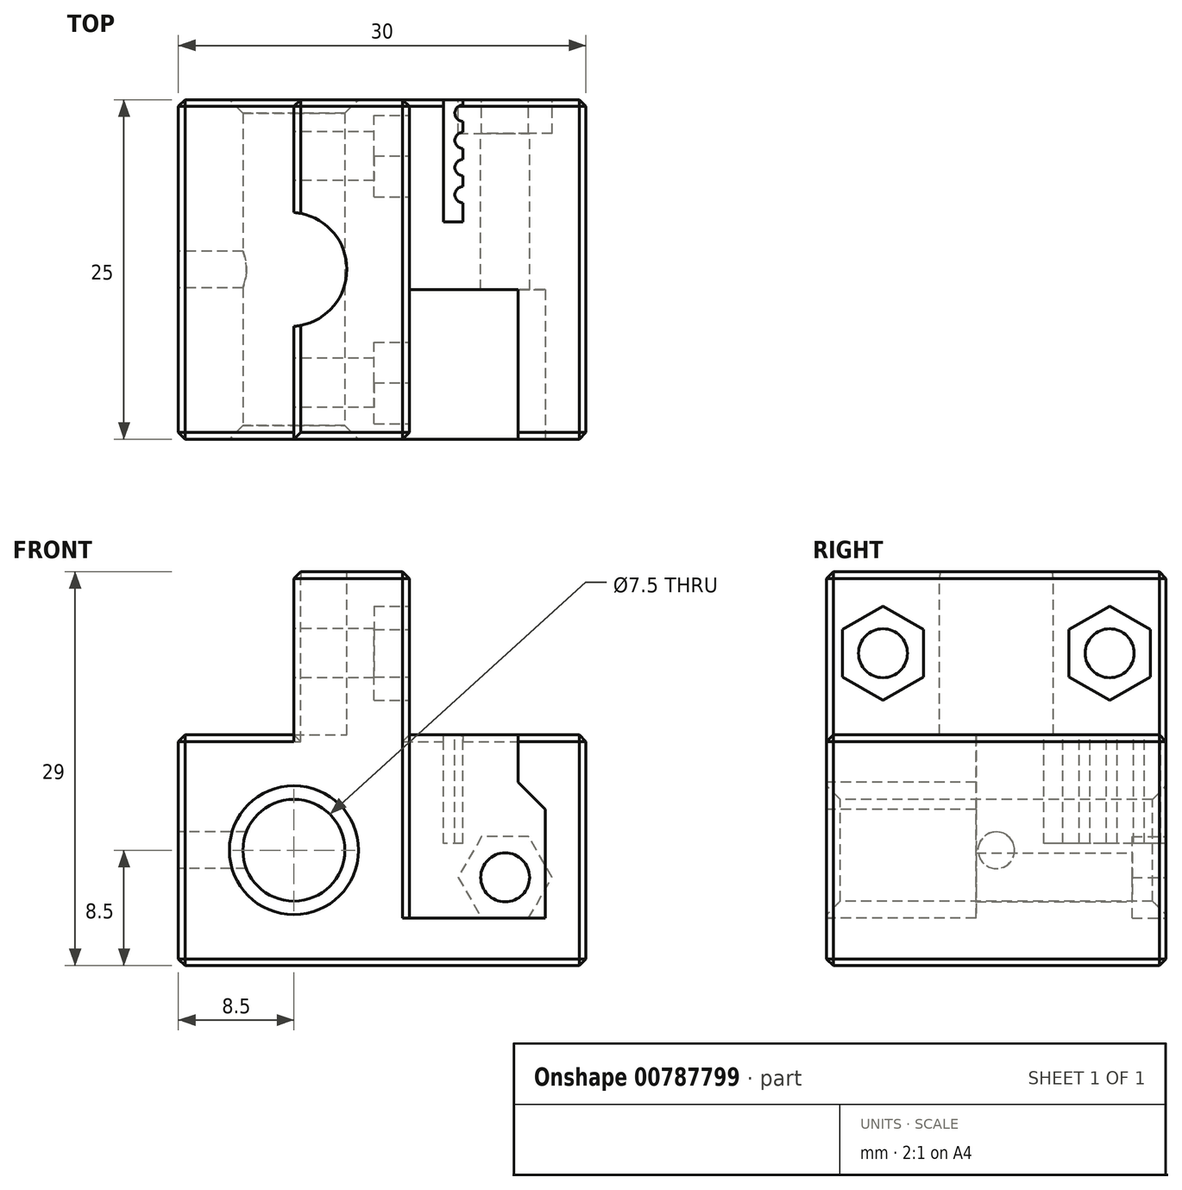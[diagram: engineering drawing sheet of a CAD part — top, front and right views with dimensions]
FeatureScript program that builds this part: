
annotation { "Feature Type Name" : "Feature", "Feature Type Description" : "" }
export const myFeature = defineFeature(function(context is Context, id is Id, definition is map)
    precondition{}
    {
        {
            var Q0;
            Q0=qCreatedBy(makeId("Top.planeOp"),FACE);
            var sketch = newSketch(context, id + "F0", { "sketchPlane" : qUnion([Q0])});
            skLineSegment(sketch, "E0.bottom", {"start": v(15, 12.5) * mm, "end": v(-15, 12.5) * mm});
            skLineSegment(sketch, "E0.top", {"start": v(15, -12.5) * mm, "end": v(-15, -12.5) * mm});
            skLineSegment(sketch, "E0.left", {"start": v(15, 12.5) * mm, "end": v(15, -12.5) * mm});
            skLineSegment(sketch, "E0.right", {"start": v(-15, 12.5) * mm, "end": v(-15, -12.5) * mm});
            skPoint(sketch, "E0.middle", {"position": v(0, 0) * mm});
            skSolve(sketch);
        }
        {
            var Q0;
            Q0=makeQuery(id+"F0.imprint","IMPRINT",FACE,{"disambiguationData":[TD([[makeQuery(id+"F0.imprint","IMPRINT",EDGE,{"derivedFrom":sQuery(id+"F0.wireOp",EDGE,"E0.bottom")}),1.0]])]});
            extrude(context, id + "F1", {"entities" : qUnion([Q0]), "depth" : 17 * mm, "offsetDistance" : 25 * mm});
        }
        {
            var Q0;
            Q0=makeQuery(id+"F1.opExtrude","SWEPT_FACE",FACE,{"disambiguationData":[OSD([sQuery(id+"F0.wireOp",EDGE,"E0.top")])]});
            var sketch = newSketch(context, id + "F2", { "sketchPlane" : qUnion([Q0])});
            skLineSegment(sketch, "E1", {"start": v(2, 17) * mm, "end": v(10, 17) * mm});
            skLineSegment(sketch, "E2", {"start": v(10, 17) * mm, "end": v(10, 13.5) * mm});
            skLineSegment(sketch, "E3", {"start": v(10, 13.5) * mm, "end": v(12, 11.5) * mm});
            skLineSegment(sketch, "E4", {"start": v(12, 11.5) * mm, "end": v(12, 3.5) * mm});
            skLineSegment(sketch, "E5", {"start": v(12, 3.5) * mm, "end": v(2, 3.5) * mm});
            skLineSegment(sketch, "E6", {"start": v(2, 3.5) * mm, "end": v(2, 17) * mm});
            skSolve(sketch);
        }
        {
            var Q0;
            Q0=makeQuery(id+"F2.imprint","IMPRINT",FACE,{"disambiguationData":[TD([[makeQuery(id+"F2.imprint","IMPRINT",EDGE,{"derivedFrom":sQuery(id+"F2.wireOp",EDGE,"E1")}),1.0]])]});
            extrude(context, id + "F3", {"entities" : qUnion([Q0]), "operationType" : NewBodyOperationType.REMOVE, "oppositeDirection" : true, "depth" : 11 * mm, "offsetDistance" : 25 * mm});
        }
        {
            var Q0;
            Q0=makeQuery(id+"F1.opExtrude","SWEPT_FACE",FACE,{"disambiguationData":[OSD([sQuery(id+"F0.wireOp",EDGE,"E0.top")])]});
            var sketch = newSketch(context, id + "F4", { "sketchPlane" : qUnion([Q0])});
            skCircle(sketch, "E7", {"center": v(-6.5, 8.5) * mm, "radius": 3.75 * mm});
            skPoint(sketch, "E7.centerSnap0", {"position": v(-6.5, 17) * mm});
            skPoint(sketch, "E7.centerSnap1", {"position": v(-15, 8.5) * mm});
            skSolve(sketch);
        }
        {
            var Q0;
            Q0=makeQuery(id+"F4.imprint","IMPRINT",FACE,{"disambiguationData":[TD([[makeQuery(id+"F4.imprint","IMPRINT",EDGE,{"derivedFrom":sQuery(id+"F4.wireOp",EDGE,"E7")}),1.0]])]});
            extrude(context, id + "F5", {"entities" : qUnion([Q0]), "operationType" : NewBodyOperationType.REMOVE, "endBound" : BoundingType.UP_TO_NEXT, "oppositeDirection" : true, "depth" : 25 * mm, "offsetDistance" : 25 * mm});
        }
        {
            var Q0;
            Q0=makeQuery(id+"F1.opExtrude","CAP_FACE",FACE,{"disambiguationData":[OSD([sQuery(id+"F0.wireOp",EDGE,"E0.bottom"),sQuery(id+"F0.wireOp",EDGE,"E0.top"),sQuery(id+"F0.wireOp",EDGE,"E0.left"),sQuery(id+"F0.wireOp",EDGE,"E0.right")])],"isStart":false});
            var sketch = newSketch(context, id + "F6", { "sketchPlane" : qUnion([Q0])});
            skLineSegment(sketch, "E8.bottom", {"start": v(2, -12.5) * mm, "end": v(-6.5, -12.5) * mm});
            skLineSegment(sketch, "E8.top", {"start": v(2, 12.5) * mm, "end": v(-6.5, 12.5) * mm});
            skLineSegment(sketch, "E8.left", {"start": v(2, -12.5) * mm, "end": v(2, 12.5) * mm});
            skLineSegment(sketch, "E8.right", {"start": v(-6.5, -12.5) * mm, "end": v(-6.5, 12.5) * mm});
            skSolve(sketch);
        }
        {
            var Q0;
            {var subQ1=sQuery(id+"F6.wireOp",EDGE,"E8.bottom");Q0=makeQuery(id+"F6.imprint","IMPRINT",FACE,{"disambiguationData":[TD([[makeQuery(id+"F6.imprint","IMPRINT",EDGE,{"derivedFrom":subQ1}),-1.0]])]});}
            extrude(context, id + "F7", {"entities" : qUnion([Q0]), "operationType" : NewBodyOperationType.ADD, "depth" : 12 * mm, "offsetDistance" : 25 * mm});
        }
        {
            var Q0;
            Q0=makeQuery(id+"F7.opExtrude","CAP_FACE",FACE,{"disambiguationData":[OSD([sQuery(id+"F6.wireOp",EDGE,"E8.bottom"),sQuery(id+"F6.wireOp",EDGE,"E8.top"),sQuery(id+"F6.wireOp",EDGE,"E8.left"),sQuery(id+"F6.wireOp",EDGE,"E8.right")])],"isStart":false});
            var sketch = newSketch(context, id + "F8", { "sketchPlane" : qUnion([Q0])});
            skArc(sketch, "E9", {"start": v(-6.5, -4.19) * mm, "mid": v(-2.6, 0) * mm, "end": v(-6.5, 4.19) * mm});
            skPoint(sketch, "E9.centerSnap0", {"position": v(-6.5, 0) * mm});
            skLineSegment(sketch, "E10", {"start": v(-6.5, 4.19) * mm, "end": v(-6.5, -4.19) * mm});
            skSolve(sketch);
        }
        {
            var Q0;
            Q0=makeQuery(id+"F8.imprint","IMPRINT",FACE,{"disambiguationData":[TD([[makeQuery(id+"F8.imprint","IMPRINT",EDGE,{"derivedFrom":sQuery(id+"F8.wireOp",EDGE,"E9")}),1.0]])]});
            extrude(context, id + "F9", {"entities" : qUnion([Q0]), "operationType" : NewBodyOperationType.REMOVE, "oppositeDirection" : true, "depth" : 12 * mm, "offsetDistance" : 25 * mm});
        }
        {
            var Q0;
            {var subQ0=sQuery(id+"F6.wireOp",EDGE,"E8.right");var subQ2=sQuery(id+"F0.wireOp",EDGE,"E0.top");Q0=makeQuery(id+"F9.boolean.opBoolean","SPLIT",FACE,{"disambiguationData":[TD([makeQuery(id+"F1.opExtrude","SWEPT_FACE",FACE,{"disambiguationData":[OSD([subQ2])]})])],"derivedFrom":makeQuery(id+"F7.opExtrude","SWEPT_FACE",FACE,{"disambiguationData":[OSD([subQ0])]})});}
            var sketch = newSketch(context, id + "F10", { "sketchPlane" : qUnion([Q0])});
            skCircle(sketch, "E11", {"center": v(8.34, 23) * mm, "radius": 1.8 * mm});
            skPoint(sketch, "E11.centerSnap0", {"position": v(12.5, 23) * mm});
            skPoint(sketch, "E11.centerSnap1", {"position": v(8.34, 29) * mm});
            skLineSegment(sketch, "E12.0", {"start": v(-4.19, 29) * mm, "end": v(-12.5, 29) * mm});
            skPoint(sketch, "E13.0", {"position": v(-4.19, 23) * mm});
            skCircle(sketch, "E14", {"center": v(-8.34, 23) * mm, "radius": 1.8 * mm});
            skPoint(sketch, "E14.centerSnap0", {"position": v(-8.34, 29) * mm});
            skSolve(sketch);
        }
        {
            var Q0;
            Q0=makeQuery(id+"F10.imprint","IMPRINT",FACE,{"disambiguationData":[TD([[makeQuery(id+"F10.imprint","IMPRINT",EDGE,{"derivedFrom":sQuery(id+"F10.wireOp",EDGE,"E14")}),1.0]])]});
            var Q1;
            Q1=makeQuery(id+"F10.imprint","IMPRINT",FACE,{"disambiguationData":[TD([[makeQuery(id+"F10.imprint","IMPRINT",EDGE,{"derivedFrom":sQuery(id+"F10.wireOp",EDGE,"E11")}),1.0]])]});
            extrude(context, id + "F11", {"entities" : qUnion([Q0, Q1]), "operationType" : NewBodyOperationType.REMOVE, "endBound" : BoundingType.UP_TO_NEXT, "oppositeDirection" : true, "depth" : 25 * mm, "offsetDistance" : 25 * mm});
        }
        {
            var Q0;
            Q0=makeQuery(id+"F7.boolean.opBoolean","MERGE",FACE,{"derivedFrom":[makeQuery(id+"F3.boolean.opBoolean","COPY",FACE,{"derivedFrom":makeQuery(id+"F3.opExtrude","SWEPT_FACE",FACE,{"disambiguationData":[OSD([sQuery(id+"F2.wireOp",EDGE,"E6")])]})}),makeQuery(id+"F7.opExtrude","SWEPT_FACE",FACE,{"disambiguationData":[OSD([sQuery(id+"F6.wireOp",EDGE,"E8.left")])]})]});
            var sketch = newSketch(context, id + "F12", { "sketchPlane" : qUnion([Q0])});
            skCircle(sketch, "E15.cCircle", {"center": v(8.34, 23) * mm, "radius": 3 * mm, "construction": true});
            skLineSegment(sketch, "E15.0", {"start": v(11.34, 24.73) * mm, "end": v(11.34, 21.27) * mm});
            skLineSegment(sketch, "E15.1", {"start": v(11.34, 21.27) * mm, "end": v(8.34, 19.54) * mm});
            skLineSegment(sketch, "E15.2", {"start": v(8.34, 19.54) * mm, "end": v(5.34, 21.27) * mm});
            skLineSegment(sketch, "E15.3", {"start": v(5.34, 21.27) * mm, "end": v(5.34, 24.73) * mm});
            skLineSegment(sketch, "E15.4", {"start": v(5.34, 24.73) * mm, "end": v(8.34, 26.46) * mm});
            skLineSegment(sketch, "E15.5", {"start": v(8.34, 26.46) * mm, "end": v(11.34, 24.73) * mm});
            skPoint(sketch, "E15.0.midPoint", {"position": v(11.34, 23) * mm});
            skCircle(sketch, "E16.cCircle", {"center": v(-8.34, 23) * mm, "radius": 3 * mm, "construction": true});
            skLineSegment(sketch, "E16.0", {"start": v(-5.34, 24.73) * mm, "end": v(-5.34, 21.27) * mm});
            skLineSegment(sketch, "E16.1", {"start": v(-5.34, 21.27) * mm, "end": v(-8.34, 19.54) * mm});
            skLineSegment(sketch, "E16.2", {"start": v(-8.34, 19.54) * mm, "end": v(-11.34, 21.27) * mm});
            skLineSegment(sketch, "E16.3", {"start": v(-11.34, 21.27) * mm, "end": v(-11.34, 24.73) * mm});
            skLineSegment(sketch, "E16.4", {"start": v(-11.34, 24.73) * mm, "end": v(-8.34, 26.46) * mm});
            skLineSegment(sketch, "E16.5", {"start": v(-8.34, 26.46) * mm, "end": v(-5.34, 24.73) * mm});
            skPoint(sketch, "E16.0.midPoint", {"position": v(-5.34, 23) * mm});
            skSolve(sketch);
        }
        {
            var Q0;
            Q0=makeQuery(id+"F12.imprint","IMPRINT",FACE,{"disambiguationData":[TD([[makeQuery(id+"F12.imprint","IMPRINT",EDGE,{"derivedFrom":sQuery(id+"F12.wireOp",EDGE,"E15.0")}),-1.0]])]});
            var Q1;
            Q1=makeQuery(id+"F12.imprint","IMPRINT",FACE,{"disambiguationData":[TD([[makeQuery(id+"F12.imprint","IMPRINT",EDGE,{"derivedFrom":sQuery(id+"F12.wireOp",EDGE,"E16.0")}),-1.0]])]});
            extrude(context, id + "F13", {"entities" : qUnion([Q0, Q1]), "operationType" : NewBodyOperationType.REMOVE, "oppositeDirection" : true, "depth" : 2.6 * mm, "offsetDistance" : 25 * mm});
        }
        {
            var Q0;
            {var subQ0=sQuery(id+"F0.wireOp",EDGE,"E0.left");var subQ1=sQuery(id+"F0.wireOp",EDGE,"E0.top");var subQ4=sQuery(id+"F0.wireOp",EDGE,"E0.bottom");Q0=makeQuery(id+"F7.boolean.opBoolean","SPLIT",FACE,{"disambiguationData":[TD([makeQuery(id+"F1.opExtrude","SWEPT_FACE",FACE,{"disambiguationData":[OSD([subQ0])]})])],"derivedFrom":makeQuery(id+"F1.opExtrude","CAP_FACE",FACE,{"disambiguationData":[OSD([subQ4,subQ1,subQ0,sQuery(id+"F0.wireOp",EDGE,"E0.right")])],"isStart":false})});}
            var sketch = newSketch(context, id + "F14", { "sketchPlane" : qUnion([Q0])});
            skLineSegment(sketch, "E17.bottom", {"start": v(4.5, 12.5) * mm, "end": v(5.95, 12.5) * mm});
            skLineSegment(sketch, "E17.top", {"start": v(4.5, 3.5) * mm, "end": v(5.95, 3.5) * mm});
            skLineSegment(sketch, "E17.left", {"start": v(4.5, 12.5) * mm, "end": v(4.5, 3.5) * mm});
            skLineSegment(sketch, "E17.right", {"start": v(5.95, 12.5) * mm, "end": v(5.95, 12.1) * mm});
            skArc(sketch, "E18", {"start": v(5.95, 12.1) * mm, "mid": v(5.35, 11.5) * mm, "end": v(5.95, 10.9) * mm});
            skArc(sketch, "E19.0.1.0", {"start": v(5.95, 10.1) * mm, "mid": v(5.35, 9.5) * mm, "end": v(5.95, 8.9) * mm});
            skArc(sketch, "E19.0.2.0", {"start": v(5.95, 8.1) * mm, "mid": v(5.35, 7.5) * mm, "end": v(5.95, 6.9) * mm});
            skArc(sketch, "E19.0.3.0", {"start": v(5.95, 6.1) * mm, "mid": v(5.35, 5.5) * mm, "end": v(5.95, 4.9) * mm});
            skLineSegment(sketch, "E19.direction1", {"start": v(5.95, 11.5) * mm, "end": v(13.56, 11.5) * mm, "construction": true});
            skLineSegment(sketch, "E19.direction2", {"start": v(5.95, 11.5) * mm, "end": v(5.95, 9.5) * mm, "construction": true});
            skLineSegment(sketch, "E20.trimOffspring", {"start": v(5.95, 4.9) * mm, "end": v(5.95, 3.5) * mm});
            skLineSegment(sketch, "E21.trimOffspring", {"start": v(5.95, 6.9) * mm, "end": v(5.95, 6.1) * mm});
            skLineSegment(sketch, "E22.trimOffspring", {"start": v(5.95, 8.9) * mm, "end": v(5.95, 8.1) * mm});
            skLineSegment(sketch, "E23.trimOffspring", {"start": v(5.95, 11.5) * mm, "end": v(5.95, 9.5) * mm});
            skSolve(sketch);
        }
        {
            var Q0;
            Q0=makeQuery(id+"F14.imprint","IMPRINT",FACE,{"disambiguationData":[TD([[makeQuery(id+"F14.imprint","IMPRINT",EDGE,{"derivedFrom":sQuery(id+"F14.wireOp",EDGE,"E17.bottom")}),1.0]])]});
            extrude(context, id + "F15", {"entities" : qUnion([Q0]), "operationType" : NewBodyOperationType.REMOVE, "oppositeDirection" : true, "depth" : 8 * mm, "offsetDistance" : 25 * mm});
        }
        {
            var Q0;
            Q0=makeQuery(id+"F7.boolean.opBoolean","MERGE",FACE,{"derivedFrom":[makeQuery(id+"F1.opExtrude","SWEPT_FACE",FACE,{"disambiguationData":[OSD([sQuery(id+"F0.wireOp",EDGE,"E0.bottom")])]}),makeQuery(id+"F7.opExtrude","SWEPT_FACE",FACE,{"disambiguationData":[OSD([sQuery(id+"F6.wireOp",EDGE,"E8.top")])]})]});
            var sketch = newSketch(context, id + "F16", { "sketchPlane" : qUnion([Q0])});
            skCircle(sketch, "E24", {"center": v(-9.05, 6.5) * mm, "radius": 1.8 * mm});
            skSolve(sketch);
        }
        {
            var Q0;
            Q0=makeQuery(id+"F16.imprint","IMPRINT",FACE,{"disambiguationData":[TD([[makeQuery(id+"F16.imprint","IMPRINT",EDGE,{"derivedFrom":sQuery(id+"F16.wireOp",EDGE,"E24")}),1.0]])]});
            extrude(context, id + "F17", {"entities" : qUnion([Q0]), "operationType" : NewBodyOperationType.REMOVE, "endBound" : BoundingType.UP_TO_NEXT, "oppositeDirection" : true, "depth" : 25 * mm, "offsetDistance" : 25 * mm});
        }
        {
            var Q0;
            Q0=makeQuery(id+"F7.boolean.opBoolean","MERGE",FACE,{"derivedFrom":[makeQuery(id+"F1.opExtrude","SWEPT_FACE",FACE,{"disambiguationData":[OSD([sQuery(id+"F0.wireOp",EDGE,"E0.bottom")])]}),makeQuery(id+"F7.opExtrude","SWEPT_FACE",FACE,{"disambiguationData":[OSD([sQuery(id+"F6.wireOp",EDGE,"E8.top")])]})]});
            var sketch = newSketch(context, id + "F18", { "sketchPlane" : qUnion([Q0])});
            skCircle(sketch, "E25.cCircle", {"center": v(-9.05, 6.5) * mm, "radius": 3 * mm, "construction": true});
            skLineSegment(sketch, "E25.0", {"start": v(-10.78, 9.5) * mm, "end": v(-7.32, 9.5) * mm});
            skLineSegment(sketch, "E25.1", {"start": v(-7.32, 9.5) * mm, "end": v(-5.59, 6.5) * mm});
            skLineSegment(sketch, "E25.2", {"start": v(-5.59, 6.5) * mm, "end": v(-7.32, 3.5) * mm});
            skLineSegment(sketch, "E25.3", {"start": v(-7.32, 3.5) * mm, "end": v(-10.78, 3.5) * mm});
            skLineSegment(sketch, "E25.4", {"start": v(-10.78, 3.5) * mm, "end": v(-12.51, 6.5) * mm});
            skLineSegment(sketch, "E25.5", {"start": v(-12.51, 6.5) * mm, "end": v(-10.78, 9.5) * mm});
            skPoint(sketch, "E25.0.midPoint", {"position": v(-9.05, 9.5) * mm});
            skSolve(sketch);
        }
        {
            var Q0;
            Q0=makeQuery(id+"F18.imprint","IMPRINT",FACE,{"disambiguationData":[TD([[makeQuery(id+"F18.imprint","IMPRINT",EDGE,{"derivedFrom":sQuery(id+"F18.wireOp",EDGE,"E25.0")}),-1.0]])]});
            extrude(context, id + "F19", {"entities" : qUnion([Q0]), "operationType" : NewBodyOperationType.REMOVE, "oppositeDirection" : true, "depth" : 2.5 * mm, "offsetDistance" : 25 * mm});
        }
        {
            var Q0;
            Q0=makeQuery(id+"F7.boolean.opBoolean","MERGE",FACE,{"derivedFrom":[makeQuery(id+"F1.opExtrude","SWEPT_FACE",FACE,{"disambiguationData":[OSD([sQuery(id+"F0.wireOp",EDGE,"E0.bottom")])]}),makeQuery(id+"F7.opExtrude","SWEPT_FACE",FACE,{"disambiguationData":[OSD([sQuery(id+"F6.wireOp",EDGE,"E8.top")])]})]});
            var sketch = newSketch(context, id + "F20", { "sketchPlane" : qUnion([Q0])});
            skCircle(sketch, "E26.0", {"center": v(6.5, 8.5) * mm, "radius": 3.75 * mm});
            skCircle(sketch, "E27", {"center": v(6.5, 8.5) * mm, "radius": 3.5 * mm});
            skLineSegment(sketch, "E28", {"start": v(5.35, 11.8) * mm, "end": v(5.29, 12.05) * mm});
            skLineSegment(sketch, "E29", {"start": v(7.65, 11.8) * mm, "end": v(7.71, 12.05) * mm});
            skLineSegment(sketch, "E30", {"start": v(6.5, -1.55) * mm, "end": v(6.5, 19.4) * mm});
            skLineSegment(sketch, "E31.1.0", {"start": v(8.79, 11.15) * mm, "end": v(8.97, 11.33) * mm});
            skLineSegment(sketch, "E31.1.1", {"start": v(9.94, 9.16) * mm, "end": v(10.18, 9.22) * mm});
            skLineSegment(sketch, "E31.2.0", {"start": v(9.94, 7.84) * mm, "end": v(10.18, 7.78) * mm});
            skLineSegment(sketch, "E31.2.1", {"start": v(8.79, 5.85) * mm, "end": v(8.97, 5.67) * mm});
            skLineSegment(sketch, "E31.3.0", {"start": v(7.65, 5.2) * mm, "end": v(7.71, 4.95) * mm});
            skLineSegment(sketch, "E31.3.1", {"start": v(5.35, 5.2) * mm, "end": v(5.29, 4.95) * mm});
            skLineSegment(sketch, "E31.4.0", {"start": v(4.21, 5.85) * mm, "end": v(4.03, 5.67) * mm});
            skLineSegment(sketch, "E31.4.1", {"start": v(3.06, 7.84) * mm, "end": v(2.82, 7.78) * mm});
            skLineSegment(sketch, "E31.5.0", {"start": v(3.06, 9.16) * mm, "end": v(2.82, 9.22) * mm});
            skLineSegment(sketch, "E31.5.1", {"start": v(4.21, 11.15) * mm, "end": v(4.03, 11.33) * mm});
            skLineSegment(sketch, "E31.anchor1", {"start": v(6.5, 8.5) * mm, "end": v(5.35, 11.8) * mm, "construction": true});
            skLineSegment(sketch, "E31.anchor2", {"start": v(6.5, 8.5) * mm, "end": v(5.35, 11.8) * mm, "construction": true});
            skSolve(sketch);
        }
        {
            var Q0;
            Q0=makeQuery(id+"F1.opExtrude","CAP_EDGE",EDGE,{"disambiguationData":[OSD([sQuery(id+"F0.wireOp",EDGE,"E0.top")])],"isStart":true});
            var Q1;
            Q1=makeQuery(id+"F1.opExtrude","CAP_EDGE",EDGE,{"disambiguationData":[OSD([sQuery(id+"F0.wireOp",EDGE,"E0.right")])],"isStart":true});
            var Q2;
            Q2=makeQuery(id+"F1.opExtrude","CAP_EDGE",EDGE,{"disambiguationData":[OSD([sQuery(id+"F0.wireOp",EDGE,"E0.bottom")])],"isStart":true});
            var Q3;
            Q3=makeQuery(id+"F1.opExtrude","CAP_EDGE",EDGE,{"disambiguationData":[OSD([sQuery(id+"F0.wireOp",EDGE,"E0.left")])],"isStart":true});
            var Q4;
            Q4=makeQuery(id+"F1.opExtrude","CAP_EDGE",EDGE,{"disambiguationData":[OSD([sQuery(id+"F0.wireOp",EDGE,"E0.right")])],"isStart":false});
            var Q5;
            {var subQ0=sQuery(id+"F0.wireOp",EDGE,"E0.right");var subQ1=sQuery(id+"F0.wireOp",EDGE,"E0.bottom");Q5=makeQuery(id+"F7.boolean.opBoolean","SPLIT",EDGE,{"disambiguationData":[TD([makeQuery(id+"F1.opExtrude","SWEPT_FACE",FACE,{"disambiguationData":[OSD([subQ0])]})])],"derivedFrom":makeQuery(id+"F1.opExtrude","CAP_EDGE",EDGE,{"disambiguationData":[OSD([subQ1])],"isStart":false})});}
            var Q6;
            Q6=makeQuery(id+"F1.opExtrude","SWEPT_EDGE",EDGE,{"disambiguationData":[OSD([sQuery(id+"F0.wireOp",EDGE,"E0.bottom"),sQuery(id+"F0.wireOp",EDGE,"E0.right")])]});
            var Q7;
            Q7=makeQuery(id+"F1.opExtrude","SWEPT_EDGE",EDGE,{"disambiguationData":[OSD([sQuery(id+"F0.wireOp",EDGE,"E0.top"),sQuery(id+"F0.wireOp",EDGE,"E0.right")])]});
            var Q8;
            Q8=makeQuery(id+"F7.boolean.opBoolean","MERGE",EDGE,{"derivedFrom":[makeQuery(id+"F3.boolean.opBoolean","COPY",EDGE,{"derivedFrom":makeQuery(id+"F3.opExtrude","CAP_EDGE",EDGE,{"disambiguationData":[OSD([sQuery(id+"F2.wireOp",EDGE,"E6")])],"isStart":true})}),makeQuery(id+"F7.opExtrude","SWEPT_EDGE",EDGE,{"disambiguationData":[OSD([sQuery(id+"F6.wireOp",EDGE,"E8.bottom"),sQuery(id+"F6.wireOp",EDGE,"E8.left")])]})]});
            var Q9;
            Q9=makeQuery(id+"F3.boolean.opBoolean","COPY",EDGE,{"derivedFrom":makeQuery(id+"F3.opExtrude","CAP_EDGE",EDGE,{"disambiguationData":[OSD([sQuery(id+"F2.wireOp",EDGE,"E5")])],"isStart":true})});
            var Q10;
            Q10=makeQuery(id+"F3.boolean.opBoolean","COPY",EDGE,{"derivedFrom":makeQuery(id+"F3.opExtrude","CAP_EDGE",EDGE,{"disambiguationData":[OSD([sQuery(id+"F2.wireOp",EDGE,"E4")])],"isStart":true})});
            var Q11;
            Q11=makeQuery(id+"F3.boolean.opBoolean","COPY",EDGE,{"derivedFrom":makeQuery(id+"F3.opExtrude","CAP_EDGE",EDGE,{"disambiguationData":[OSD([sQuery(id+"F2.wireOp",EDGE,"E3")])],"isStart":true})});
            var Q12;
            Q12=makeQuery(id+"F3.boolean.opBoolean","COPY",EDGE,{"derivedFrom":makeQuery(id+"F3.opExtrude","CAP_EDGE",EDGE,{"disambiguationData":[OSD([sQuery(id+"F2.wireOp",EDGE,"E2")])],"isStart":true})});
            var Q13;
            Q13=makeQuery(id+"F1.opExtrude","SWEPT_EDGE",EDGE,{"disambiguationData":[OSD([sQuery(id+"F0.wireOp",EDGE,"E0.top"),sQuery(id+"F0.wireOp",EDGE,"E0.left")])]});
            var Q14;
            {var subQ0=sQuery(id+"F0.wireOp",EDGE,"E0.left");var subQ1=sQuery(id+"F0.wireOp",EDGE,"E0.top");Q14=makeQuery(id+"F3.boolean.opBoolean","SPLIT",EDGE,{"disambiguationData":[TD([makeQuery(id+"F1.opExtrude","SWEPT_FACE",FACE,{"disambiguationData":[OSD([subQ0])]})])],"derivedFrom":makeQuery(id+"F1.opExtrude","CAP_EDGE",EDGE,{"disambiguationData":[OSD([subQ1])],"isStart":false})});}
            var Q15;
            Q15=makeQuery(id+"F1.opExtrude","CAP_EDGE",EDGE,{"disambiguationData":[OSD([sQuery(id+"F0.wireOp",EDGE,"E0.left")])],"isStart":false});
            var Q16;
            Q16=makeQuery(id+"F1.opExtrude","SWEPT_EDGE",EDGE,{"disambiguationData":[OSD([sQuery(id+"F0.wireOp",EDGE,"E0.bottom"),sQuery(id+"F0.wireOp",EDGE,"E0.left")])]});
            var Q17;
            {var subQ0=sQuery(id+"F0.wireOp",EDGE,"E0.left");var subQ1=makeQuery(id+"F1.opExtrude","SWEPT_FACE",FACE,{"disambiguationData":[OSD([subQ0])]});var subQ2=sQuery(id+"F0.wireOp",EDGE,"E0.bottom");Q17=makeQuery(id+"F15.boolean.opBoolean","SPLIT",EDGE,{"disambiguationData":[TD([subQ1])],"derivedFrom":makeQuery(id+"F7.boolean.opBoolean","SPLIT",EDGE,{"disambiguationData":[TD([subQ1])],"derivedFrom":makeQuery(id+"F1.opExtrude","CAP_EDGE",EDGE,{"disambiguationData":[OSD([subQ2])],"isStart":false})})});}
            var Q18;
            {var subQ0=sQuery(id+"F0.wireOp",EDGE,"E0.left");var subQ1=sQuery(id+"F0.wireOp",EDGE,"E0.bottom");var subQ4=makeQuery(id+"F3.boolean.opBoolean","COPY",FACE,{"derivedFrom":makeQuery(id+"F3.opExtrude","SWEPT_FACE",FACE,{"disambiguationData":[OSD([sQuery(id+"F2.wireOp",EDGE,"E6")])]})});Q18=makeQuery(id+"F15.boolean.opBoolean","SPLIT",EDGE,{"disambiguationData":[TD([subQ4])],"derivedFrom":makeQuery(id+"F7.boolean.opBoolean","SPLIT",EDGE,{"disambiguationData":[TD([makeQuery(id+"F1.opExtrude","SWEPT_FACE",FACE,{"disambiguationData":[OSD([subQ0])]})])],"derivedFrom":makeQuery(id+"F1.opExtrude","CAP_EDGE",EDGE,{"disambiguationData":[OSD([subQ1])],"isStart":false})})});}
            var Q19;
            Q19=makeQuery(id+"F7.opExtrude","SWEPT_EDGE",EDGE,{"disambiguationData":[OSD([sQuery(id+"F0.wireOp",EDGE,"E0.bottom"),sQuery(id+"F6.wireOp",EDGE,"E8.top"),sQuery(id+"F6.wireOp",EDGE,"E8.left")])]});
            var Q20;
            Q20=makeQuery(id+"F7.opExtrude","SWEPT_EDGE",EDGE,{"disambiguationData":[OSD([sQuery(id+"F0.wireOp",EDGE,"E0.bottom"),sQuery(id+"F6.wireOp",EDGE,"E8.top"),sQuery(id+"F6.wireOp",EDGE,"E8.right")])]});
            var Q21;
            Q21=makeQuery(id+"F7.opExtrude","CAP_EDGE",EDGE,{"disambiguationData":[OSD([sQuery(id+"F6.wireOp",EDGE,"E8.top")])],"isStart":false});
            var Q22;
            Q22=makeQuery(id+"F7.opExtrude","CAP_EDGE",EDGE,{"disambiguationData":[OSD([sQuery(id+"F6.wireOp",EDGE,"E8.left")])],"isStart":false});
            var Q23;
            Q23=makeQuery(id+"F7.opExtrude","CAP_EDGE",EDGE,{"disambiguationData":[OSD([sQuery(id+"F6.wireOp",EDGE,"E8.bottom")])],"isStart":false});
            var Q24;
            {var subQ0=sQuery(id+"F0.wireOp",EDGE,"E0.right");var subQ1=sQuery(id+"F0.wireOp",EDGE,"E0.top");Q24=makeQuery(id+"F3.boolean.opBoolean","SPLIT",EDGE,{"disambiguationData":[TD([makeQuery(id+"F1.opExtrude","SWEPT_FACE",FACE,{"disambiguationData":[OSD([subQ0])]})])],"derivedFrom":makeQuery(id+"F1.opExtrude","CAP_EDGE",EDGE,{"disambiguationData":[OSD([subQ1])],"isStart":false})});}
            var Q25;
            {var subQ0=sQuery(id+"F6.wireOp",EDGE,"E8.right");Q25=makeQuery(id+"F9.boolean.opBoolean","SPLIT",EDGE,{"disambiguationData":[TD([makeQuery(id+"F1.opExtrude","SWEPT_FACE",FACE,{"disambiguationData":[OSD([sQuery(id+"F0.wireOp",EDGE,"E0.top")])]})])],"derivedFrom":makeQuery(id+"F7.opExtrude","CAP_EDGE",EDGE,{"disambiguationData":[OSD([subQ0])],"isStart":false})});}
            var Q26;
            Q26=makeQuery(id+"F9.boolean.opBoolean","COPY",EDGE,{"derivedFrom":makeQuery(id+"F9.opExtrude","CAP_EDGE",EDGE,{"disambiguationData":[OSD([sQuery(id+"F8.wireOp",EDGE,"E9")])],"isStart":true})});
            var Q27;
            {var subQ0=sQuery(id+"F6.wireOp",EDGE,"E8.right");Q27=makeQuery(id+"F9.boolean.opBoolean","SPLIT",EDGE,{"disambiguationData":[TD([makeQuery(id+"F1.opExtrude","SWEPT_FACE",FACE,{"disambiguationData":[OSD([sQuery(id+"F0.wireOp",EDGE,"E0.bottom")])]})])],"derivedFrom":makeQuery(id+"F7.opExtrude","CAP_EDGE",EDGE,{"disambiguationData":[OSD([subQ0])],"isStart":false})});}
            chamfer(context, id + "F21", {"entities" : qUnion([Q0, Q1, Q2, Q3, Q4, Q5, Q6, Q7, Q8, Q9, Q10, Q11, Q12, Q13, Q14, Q15, Q16, Q17, Q18, Q19, Q20, Q21, Q22, Q23, Q24, Q25, Q26, Q27]), "width" : 0.5 * mm, "tangentPropagation" : true});
        }
        {
            var Q0;
            Q0=makeQuery(id+"F5.boolean.opBoolean","COPY",FACE,{"derivedFrom":makeQuery(id+"F5.opExtrude","SWEPT_FACE",FACE,{"disambiguationData":[OSD([sQuery(id+"F4.wireOp",EDGE,"E7")])]})});
            chamfer(context, id + "F22", {"entities" : qUnion([Q0]), "chamferType" : ChamferType.OFFSET_ANGLE, "width" : 1 * mm, "oppositeDirection" : false, "angle" : 45 * degree, "tangentPropagation" : true});
        }
        {
            var Q0;
            Q0=makeQuery(id+"F1.opExtrude","SWEPT_FACE",FACE,{"disambiguationData":[OSD([sQuery(id+"F0.wireOp",EDGE,"E0.right")])]});
            var sketch = newSketch(context, id + "F23", { "sketchPlane" : qUnion([Q0])});
            skCircle(sketch, "E32", {"center": v(0, 8.5) * mm, "radius": 1.35 * mm});
            skPoint(sketch, "E32.centerSnap0", {"position": v(12, 8.5) * mm});
            skSolve(sketch);
        }
        {
            var Q0;
            Q0=makeQuery(id+"F23.imprint","IMPRINT",FACE,{"disambiguationData":[TD([[makeQuery(id+"F23.imprint","IMPRINT",EDGE,{"derivedFrom":sQuery(id+"F23.wireOp",EDGE,"E32")}),1.0]])]});
            extrude(context, id + "F24", {"entities" : qUnion([Q0]), "operationType" : NewBodyOperationType.REMOVE, "endBound" : BoundingType.UP_TO_NEXT, "oppositeDirection" : true, "depth" : 25 * mm, "offsetDistance" : 25 * mm});
        }
    });
